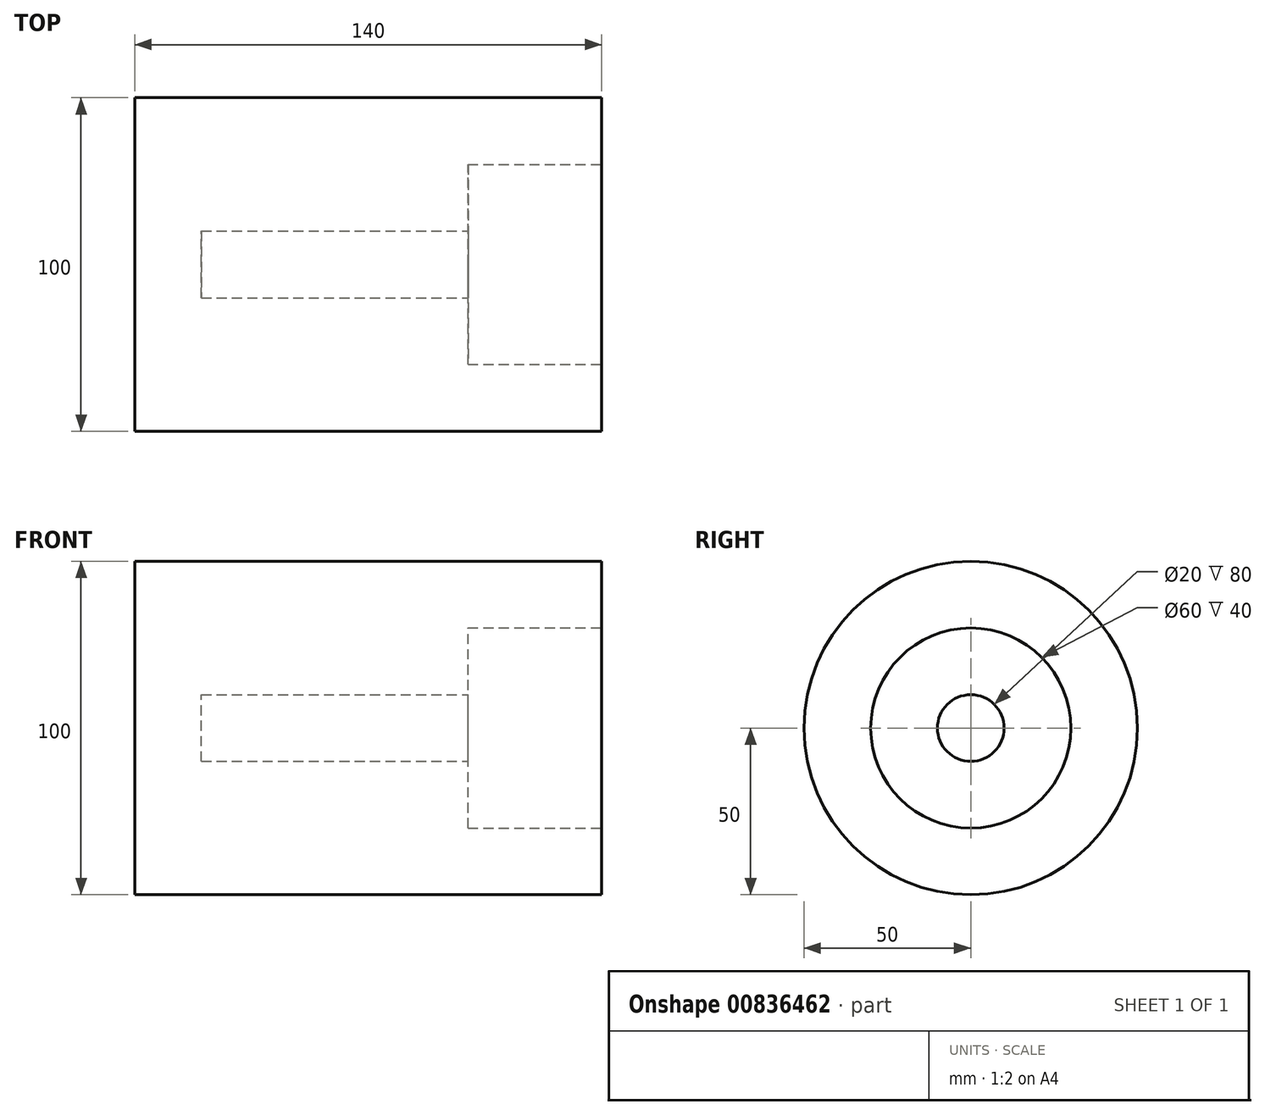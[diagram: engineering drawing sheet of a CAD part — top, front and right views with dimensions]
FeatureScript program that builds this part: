
annotation { "Feature Type Name" : "Feature", "Feature Type Description" : "" }
export const myFeature = defineFeature(function(context is Context, id is Id, definition is map)
    precondition{}
    {
        {
            var Q0;
            Q0=qCreatedBy(makeId("Top.planeOp"),FACE);
            var sketch = newSketch(context, id + "F0", { "sketchPlane" : qUnion([Q0])});
            skLineSegment(sketch, "E0.bottom", {"start": v(70, 50) * mm, "end": v(-70, 50) * mm});
            skLineSegment(sketch, "E0.left", {"start": v(70, 50) * mm, "end": v(70, 30) * mm});
            skLineSegment(sketch, "E0.right", {"start": v(-70, 50) * mm, "end": v(-70, 0) * mm});
            skPoint(sketch, "E0.middle", {"position": v(0, 25) * mm});
            skLineSegment(sketch, "E1.top", {"start": v(70, 30) * mm, "end": v(30, 30) * mm});
            skLineSegment(sketch, "E1.right", {"start": v(30, 10) * mm, "end": v(30, 30) * mm});
            skLineSegment(sketch, "E2.top", {"start": v(30, 10) * mm, "end": v(-50, 10) * mm});
            skLineSegment(sketch, "E2.right", {"start": v(-50, 0) * mm, "end": v(-50, 10) * mm});
            skLineSegment(sketch, "E3.trimOffspring", {"start": v(-50, 0) * mm, "end": v(-70, 0) * mm});
            skPoint(sketch, "E4.orphan", {"position": v(70, 0) * mm});
            skSolve(sketch);
        }
        {
            var Q0;
            Q0=makeQuery(id+"F0.imprint","IMPRINT",FACE,{"disambiguationData":[TD([[makeQuery(id+"F0.imprint","IMPRINT",EDGE,{"derivedFrom":sQuery(id+"F0.wireOp",EDGE,"E0.bottom")}),1.0]])]});
            var Q1;
            Q1=sQuery(id+"F0.wireOp",EDGE,"E3.trimOffspring");
            revolve(context, id + "F1", {"surfaceOperationType" : NewSurfaceOperationType.NEW, "entities" : qUnion([Q0]), "axis" : qUnion([Q1]), "revolveType" : RevolveType.FULL});
        }
    });
